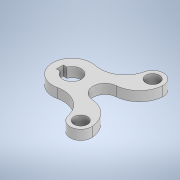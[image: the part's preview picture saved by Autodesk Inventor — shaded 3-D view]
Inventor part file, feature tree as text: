
AUTODESK INVENTOR PART (.ipt)
format: ipt  version: 2021 (Build 250183000, 183)  size: 150,016 bytes
history: native  units: mm
features: extrude x1, sketch x1
ambient origin geometry x8: Origin, YZ Plane, XZ Plane, XY Plane, X Axis, Y Axis, Z Axis, Center Point
bodies: Solid1 (feature_tree)
feature tree (2):
  extrude  "Extrusion1"  Depth=50.0mm
  sketch  "Sketch1"  dims[d0=200.0mm d1=124.0mm d2=170.0mm d3=110.0mm d4=110.0mm d5=370.0mm d6=185.0mm d7=260.0mm d8=230.0mm d9=0.0mm d10=260.0mm d11=0.0mm d12=260.0mm d13=260.0mm d14=70.0mm d15=70.0mm d16=95.0mm d17=35.0mm d18=17.5mm d19=62.5mm d20=50.0mm d21=0.0mm]
